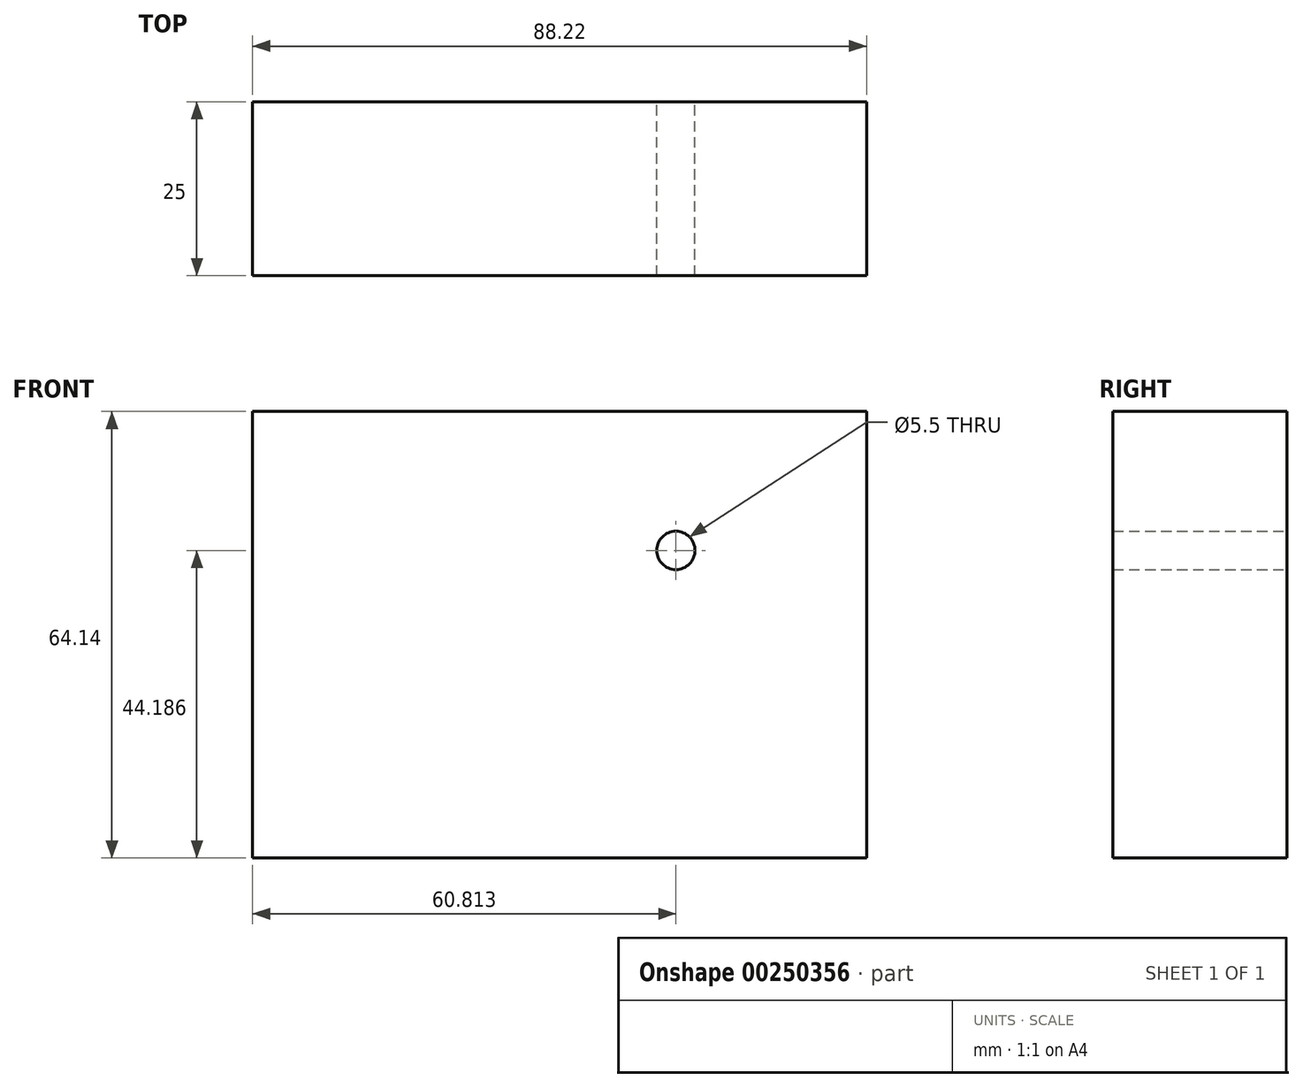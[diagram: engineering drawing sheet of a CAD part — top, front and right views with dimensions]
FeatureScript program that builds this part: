
annotation { "Feature Type Name" : "Feature", "Feature Type Description" : "" }
export const myFeature = defineFeature(function(context is Context, id is Id, definition is map)
    precondition{}
    {
        {
            var Q0;
            Q0=qCreatedBy(makeId("Front.planeOp"),FACE);
            var sketch = newSketch(context, id + "F0", { "sketchPlane" : qUnion([Q0])});
            skLineSegment(sketch, "E0.bottom", {"start": v(44.11, 32.07) * mm, "end": v(-44.11, 32.07) * mm});
            skLineSegment(sketch, "E0.top", {"start": v(44.11, -32.07) * mm, "end": v(-44.11, -32.07) * mm});
            skLineSegment(sketch, "E0.left", {"start": v(44.11, 32.07) * mm, "end": v(44.11, -32.07) * mm});
            skLineSegment(sketch, "E0.right", {"start": v(-44.11, 32.07) * mm, "end": v(-44.11, -32.07) * mm});
            skPoint(sketch, "E0.middle", {"position": v(0, 0) * mm});
            skSolve(sketch);
        }
        {
            var Q0;
            Q0=makeQuery(id+"F0.imprint","IMPRINT",FACE,{"disambiguationData":[TD([[makeQuery(id+"F0.imprint","IMPRINT",EDGE,{"derivedFrom":sQuery(id+"F0.wireOp",EDGE,"E0.bottom")}),1.0]])]});
            extrude(context, id + "F1", {"entities" : qUnion([Q0]), "depth" : 25 * mm});
        }
        {
            var Q0;
            Q0=makeQuery(id+"F1.opExtrude","CAP_FACE",FACE,{"disambiguationData":[OSD([sQuery(id+"F0.wireOp",EDGE,"E0.bottom"),sQuery(id+"F0.wireOp",EDGE,"E0.top"),sQuery(id+"F0.wireOp",EDGE,"E0.left"),sQuery(id+"F0.wireOp",EDGE,"E0.right")])],"isStart":true});
            var sketch = newSketch(context, id + "F2", { "sketchPlane" : qUnion([Q0])});
            skPoint(sketch, "E1", {"position": v(-16.7, 12.12) * mm});
            skSolve(sketch);
        }
        {
            var Q0;
            Q0=sQuery(id+"F2.wireOp",VERTEX,"E1");
            var Q1;
            Q1=makeQuery(id+"F1.opExtrude","SWEPT_BODY",BODY,{"disambiguationData":[OSD([sQuery(id+"F0.wireOp",EDGE,"E0.bottom"),sQuery(id+"F0.wireOp",EDGE,"E0.top"),sQuery(id+"F0.wireOp",EDGE,"E0.left"),sQuery(id+"F0.wireOp",EDGE,"E0.right")])]});
            hole(context, id + "F3", {"style" : HoleStyle.SIMPLE, "endStyle" : HoleEndStyle.THROUGH, "standardTappedOrClearance" : lookupTablePath({ "standard" : "ISO", "fit" : "Normal", "size" : "M5", "type" : "Clearance" }), "standardBlindInLast" : lookupTablePath({ "fit" : "Standard", "standard" : "ISO", "size" : "M5", "type" : "Clearance" }), "holeDiameter" : 5.5 * mm, "tappedDepth" : 12 * mm, "tapClearance" : 3, "locations" : qUnion([Q0]), "scope" : qUnion([Q1])});
        }
    });
